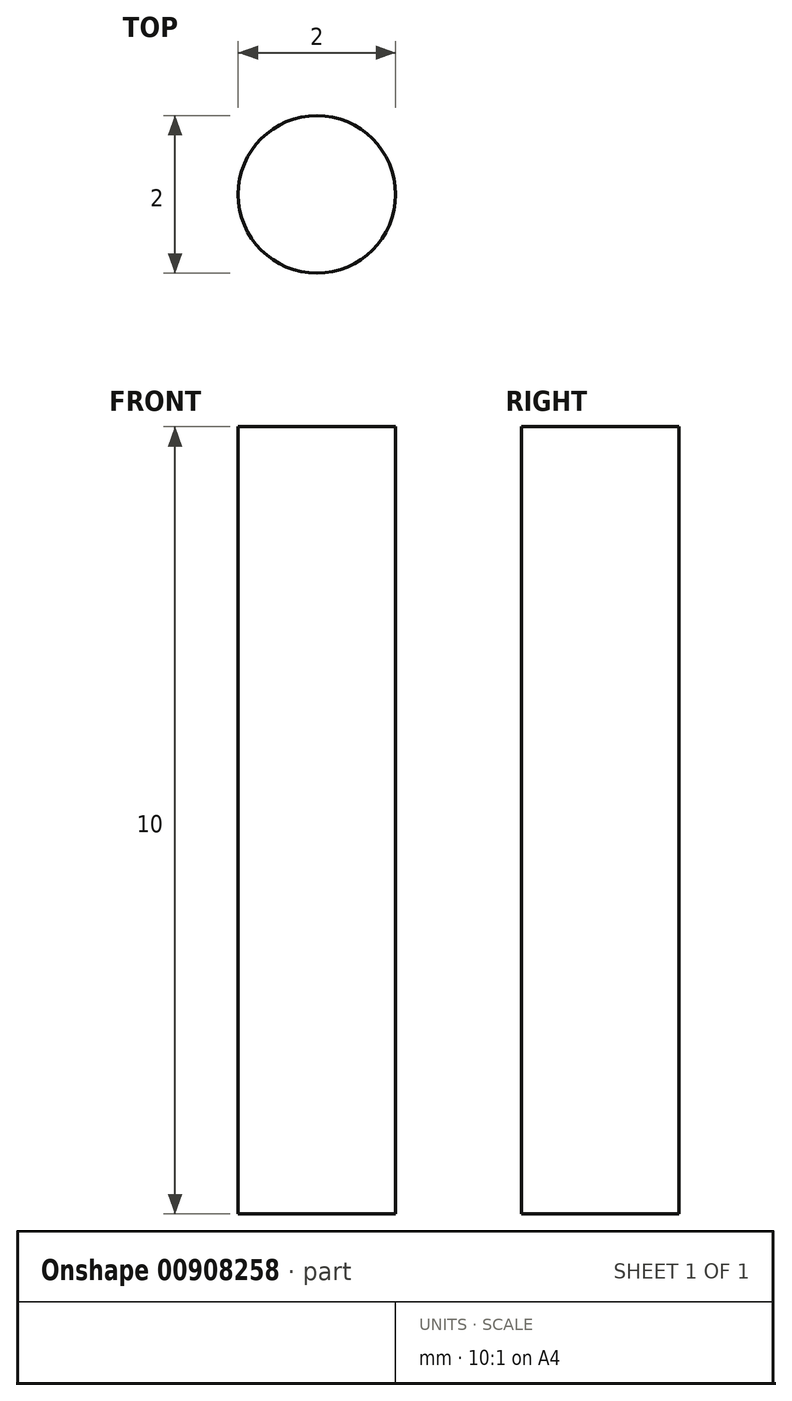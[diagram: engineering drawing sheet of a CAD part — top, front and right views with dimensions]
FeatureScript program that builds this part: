
annotation { "Feature Type Name" : "Feature", "Feature Type Description" : "" }
export const myFeature = defineFeature(function(context is Context, id is Id, definition is map)
    precondition{}
    {
        {
            var Q0;
            Q0=qCreatedBy(makeId("Top.planeOp"),FACE);
            var sketch = newSketch(context, id + "F0", { "sketchPlane" : qUnion([Q0])});
            skCircle(sketch, "E0", {"center": v(0, 0) * mm, "radius": 1 * mm});
            skSolve(sketch);
        }
        {
            var Q0;
            Q0=makeQuery(id+"F0.imprint","IMPRINT",FACE,{"disambiguationData":[TD([[makeQuery(id+"F0.imprint","IMPRINT",EDGE,{"derivedFrom":sQuery(id+"F0.wireOp",EDGE,"E0")}),1.0]])]});
            extrude(context, id + "F1", {"entities" : qUnion([Q0]), "depth" : 10 * mm, "offsetDistance" : 25 * mm});
        }
    });
